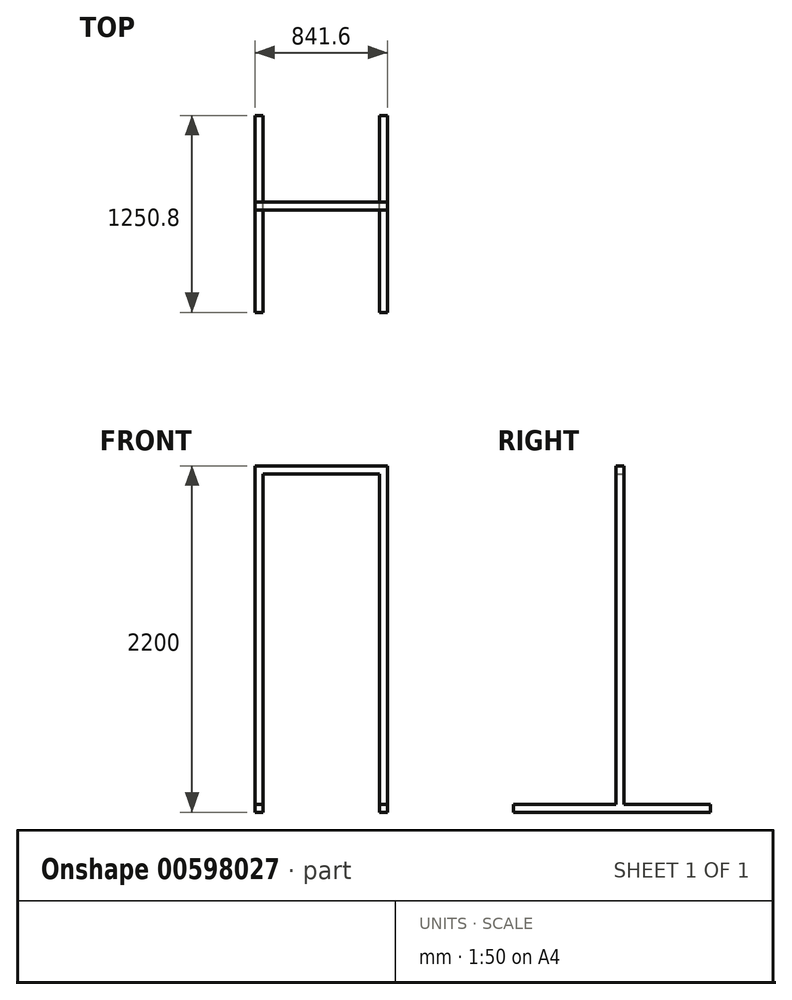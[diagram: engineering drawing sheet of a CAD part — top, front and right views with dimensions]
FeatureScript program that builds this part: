
annotation { "Feature Type Name" : "Feature", "Feature Type Description" : "" }
export const myFeature = defineFeature(function(context is Context, id is Id, definition is map)
    precondition{}
    {
        {
            var Q0;
            Q0=qCreatedBy(makeId("Front.planeOp"),FACE);
            var sketch = newSketch(context, id + "F0", { "sketchPlane" : qUnion([Q0])});
            skLineSegment(sketch, "E0.bottom", {"start": v(-338.24, -282.96) * mm, "end": v(-287.44, -282.96) * mm});
            skLineSegment(sketch, "E0.top", {"start": v(-338.24, 1866.24) * mm, "end": v(-287.44, 1866.24) * mm});
            skLineSegment(sketch, "E0.left", {"start": v(-338.24, -282.96) * mm, "end": v(-338.24, 1866.24) * mm});
            skLineSegment(sketch, "E0.right", {"start": v(-287.44, -282.96) * mm, "end": v(-287.44, 1866.24) * mm});
            skLineSegment(sketch, "E1.bottom", {"start": v(-338.24, 1866.24) * mm, "end": v(503.36, 1866.24) * mm});
            skLineSegment(sketch, "E1.top", {"start": v(-338.24, 1917.04) * mm, "end": v(503.36, 1917.04) * mm});
            skLineSegment(sketch, "E1.left", {"start": v(-338.24, 1866.24) * mm, "end": v(-338.24, 1917.04) * mm});
            skLineSegment(sketch, "E1.right", {"start": v(503.36, 1866.24) * mm, "end": v(503.36, 1917.04) * mm});
            skLineSegment(sketch, "E2.bottom", {"start": v(503.36, 1917.04) * mm, "end": v(452.56, 1917.04) * mm});
            skLineSegment(sketch, "E2.top", {"start": v(503.36, -282.96) * mm, "end": v(452.56, -282.96) * mm});
            skLineSegment(sketch, "E2.left", {"start": v(503.36, 1917.04) * mm, "end": v(503.36, -282.96) * mm});
            skLineSegment(sketch, "E2.right", {"start": v(452.56, 1917.04) * mm, "end": v(452.56, -282.96) * mm});
            skSolve(sketch);
        }
        {
            var Q0;
            Q0 = qSketchRegion(id + "F0", true);
            extrude(context, id + "F1", {"entities" : qUnion([Q0]), "depth" : 50.8 * mm, "offsetDistance" : 25.4 * mm});
        }
        {
            var Q0;
            Q0=makeQuery(id+"F1.opExtrude","CAP_FACE",FACE,{"disambiguationData":[OSD([sQuery(id+"F0.wireOp",EDGE,"E0.bottom"),sQuery(id+"F0.wireOp",EDGE,"E0.left"),sQuery(id+"F0.wireOp",EDGE,"E0.right"),sQuery(id+"F0.wireOp",EDGE,"E1.bottom"),sQuery(id+"F0.wireOp",EDGE,"E1.top"),sQuery(id+"F0.wireOp",EDGE,"E1.left"),sQuery(id+"F0.wireOp",EDGE,"E2.bottom"),sQuery(id+"F0.wireOp",EDGE,"E2.top"),sQuery(id+"F0.wireOp",EDGE,"E2.left"),sQuery(id+"F0.wireOp",EDGE,"E2.right")])],"isStart":false});
            var sketch = newSketch(context, id + "F2", { "sketchPlane" : qUnion([Q0])});
            skLineSegment(sketch, "E3.bottom", {"start": v(-338.24, -282.96) * mm, "end": v(-287.44, -282.96) * mm});
            skLineSegment(sketch, "E3.top", {"start": v(-338.24, -232.16) * mm, "end": v(-287.44, -232.16) * mm});
            skLineSegment(sketch, "E3.left", {"start": v(-338.24, -282.96) * mm, "end": v(-338.24, -232.16) * mm});
            skLineSegment(sketch, "E3.right", {"start": v(-287.44, -282.96) * mm, "end": v(-287.44, -232.16) * mm});
            skLineSegment(sketch, "E4.bottom", {"start": v(452.56, -282.96) * mm, "end": v(503.36, -282.96) * mm});
            skLineSegment(sketch, "E4.top", {"start": v(452.56, -232.16) * mm, "end": v(503.36, -232.16) * mm});
            skLineSegment(sketch, "E4.left", {"start": v(452.56, -282.96) * mm, "end": v(452.56, -232.16) * mm});
            skLineSegment(sketch, "E4.right", {"start": v(503.36, -282.96) * mm, "end": v(503.36, -232.16) * mm});
            skSolve(sketch);
        }
        {
            var Q0;
            Q0 = qSketchRegion(id + "F2", true);
            extrude(context, id + "F3", {"entities" : qUnion([Q0]), "operationType" : NewBodyOperationType.ADD, "depth" : 650.8 * mm, "offsetDistance" : 25.4 * mm, "hasSecondDirection" : true, "secondDirectionOppositeDirection" : true, "secondDirectionDepth" : 600 * mm});
        }
    });
